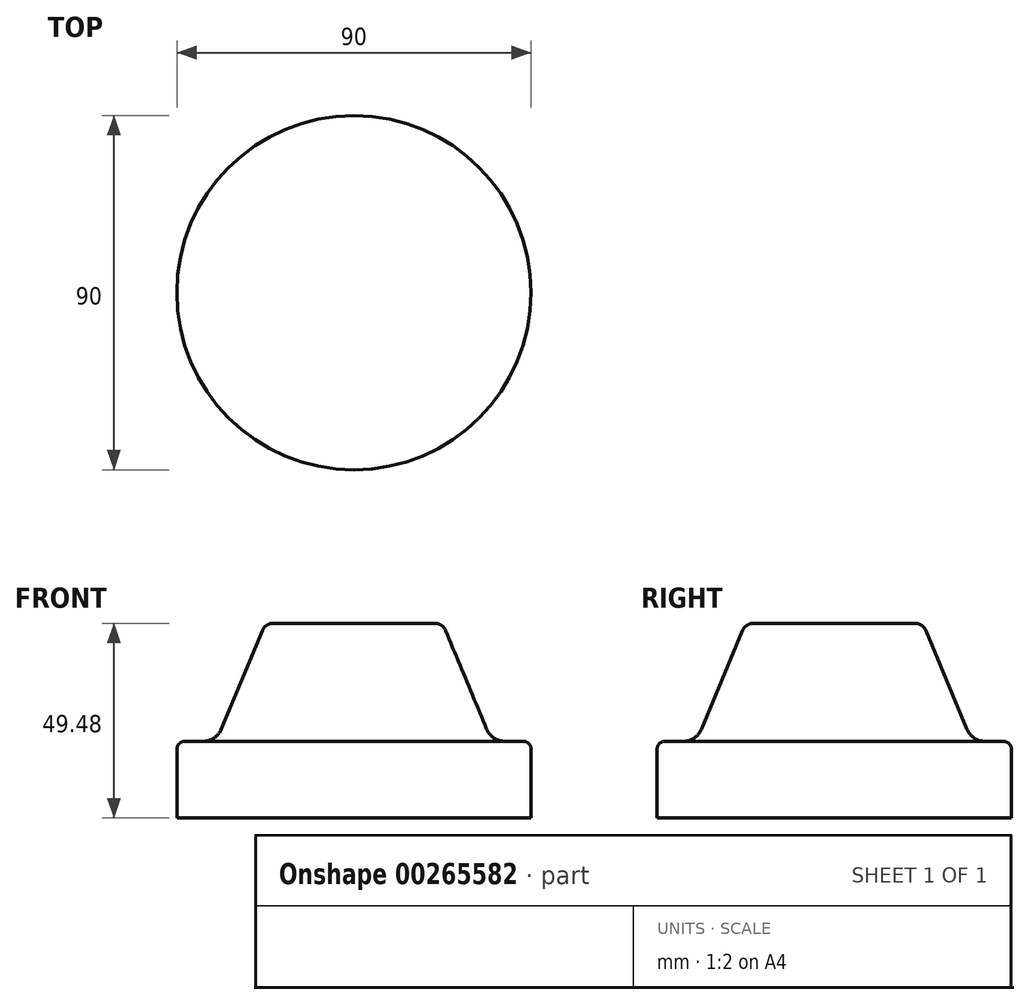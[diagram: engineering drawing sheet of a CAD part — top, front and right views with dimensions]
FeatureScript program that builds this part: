
annotation { "Feature Type Name" : "Feature", "Feature Type Description" : "" }
export const myFeature = defineFeature(function(context is Context, id is Id, definition is map)
    precondition{}
    {
        {
            var Q0;
            Q0=qCreatedBy(makeId("Front.planeOp"),FACE);
            var sketch = newSketch(context, id + "F0", { "sketchPlane" : qUnion([Q0])});
            skLineSegment(sketch, "E0", {"start": v(0, 50) * mm, "end": v(0, 0) * mm});
            skLineSegment(sketch, "E1", {"start": v(0, 0) * mm, "end": v(45, 0) * mm});
            skLineSegment(sketch, "E2", {"start": v(45, 0) * mm, "end": v(45, 17.48) * mm});
            skLineSegment(sketch, "E3", {"start": v(43, 19.48) * mm, "end": v(38.33, 19.48) * mm});
            skLineSegment(sketch, "E4", {"start": v(33.72, 22.55) * mm, "end": v(23.27, 47.63) * mm});
            skLineSegment(sketch, "E5", {"start": v(20.5, 49.48) * mm, "end": v(0, 49.48) * mm});
            skPoint(sketch, "E6.visualSharp", {"position": v(22.5, 49.48) * mm});
            skArc(sketch, "E6.filletArc", {"start": v(23.27, 47.63) * mm, "mid": v(22.16, 48.97) * mm, "end": v(20.5, 49.48) * mm});
            skPoint(sketch, "E7.visualSharp", {"position": v(35, 19.48) * mm});
            skArc(sketch, "E7.filletArc", {"start": v(33.72, 22.55) * mm, "mid": v(35.56, 20.31) * mm, "end": v(38.33, 19.48) * mm});
            skPoint(sketch, "E8.visualSharp", {"position": v(45, 19.48) * mm});
            skArc(sketch, "E8.filletArc", {"start": v(45, 17.48) * mm, "mid": v(44.41, 18.89) * mm, "end": v(43, 19.48) * mm});
            skLineSegment(sketch, "E9", {"start": v(0, 61.2) * mm, "end": v(0, -27.35) * mm, "construction": true});
            skSolve(sketch);
        }
        {
            var Q0;
            Q0 = qSketchRegion(id + "F0", true);
            var Q1;
            Q1=sQuery(id+"F0.wireOp",EDGE,"E9");
            revolve(context, id + "F1", {"entities" : qUnion([Q0]), "axis" : qUnion([Q1]), "revolveType" : RevolveType.FULL});
        }
    });
